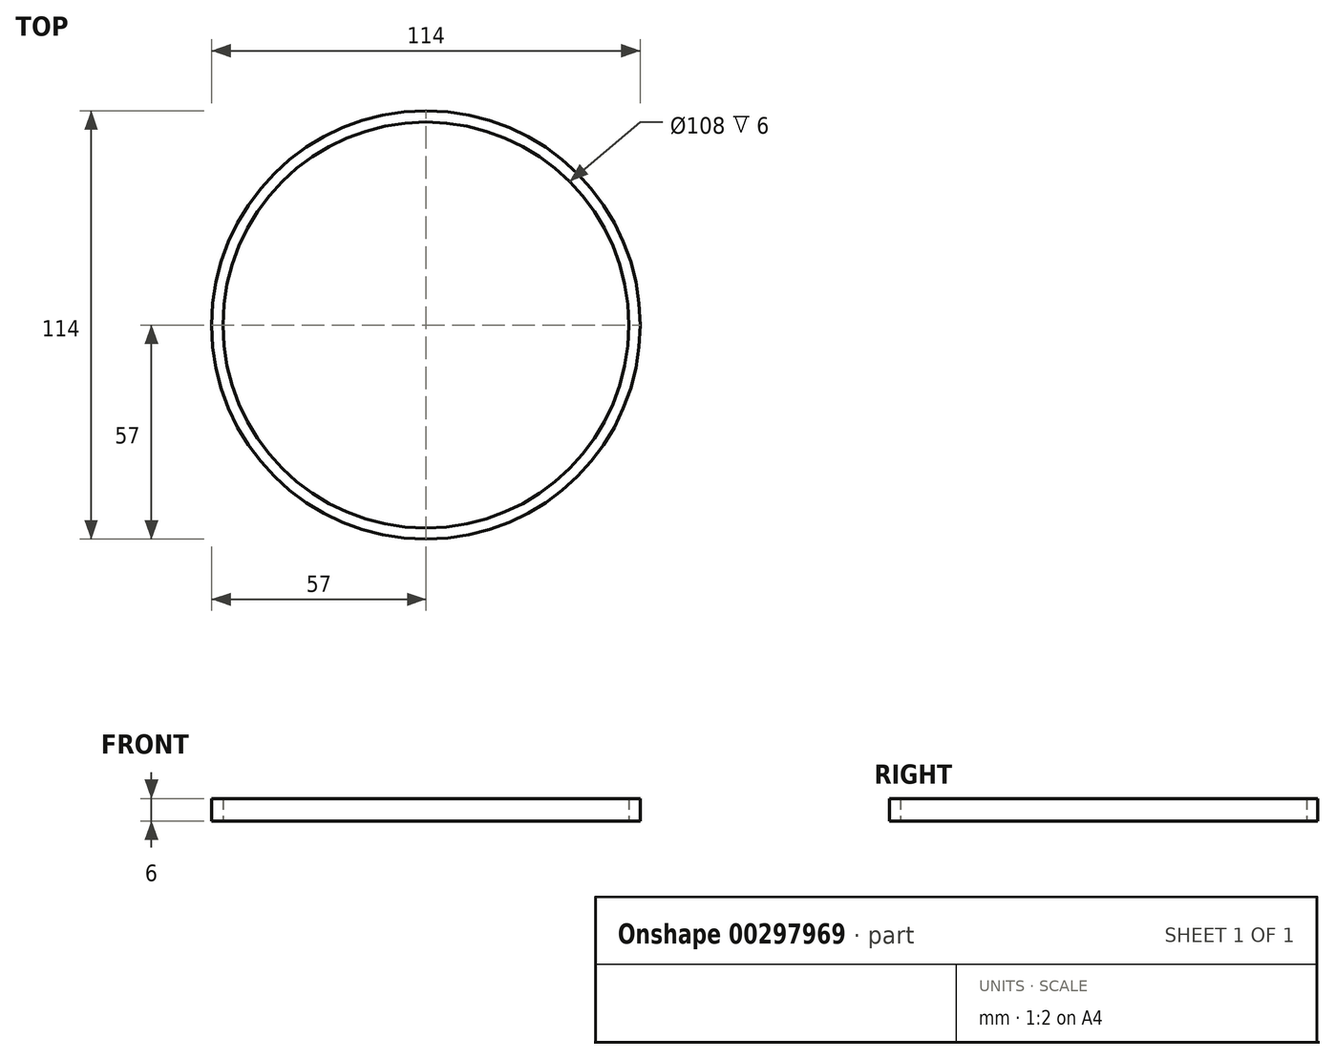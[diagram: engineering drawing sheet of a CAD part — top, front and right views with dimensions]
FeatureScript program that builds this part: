
annotation { "Feature Type Name" : "Feature", "Feature Type Description" : "" }
export const myFeature = defineFeature(function(context is Context, id is Id, definition is map)
    precondition{}
    {
        {
            var Q0;
            Q0=qCreatedBy(makeId("Front.planeOp"),FACE);
            var sketch = newSketch(context, id + "F0", { "sketchPlane" : qUnion([Q0])});
            skLineSegment(sketch, "E0.bottom", {"start": v(54, 0) * mm, "end": v(57, 0) * mm});
            skLineSegment(sketch, "E0.top", {"start": v(54, 6) * mm, "end": v(57, 6) * mm});
            skLineSegment(sketch, "E0.left", {"start": v(54, 0) * mm, "end": v(54, 6) * mm});
            skLineSegment(sketch, "E0.right", {"start": v(57, 0) * mm, "end": v(57, 6) * mm});
            skLineSegment(sketch, "E1", {"start": v(0, -8.33) * mm, "end": v(0, 13.44) * mm, "construction": true});
            skSolve(sketch);
        }
        {
            var Q0;
            Q0=makeQuery(id+"F0.imprint","IMPRINT",FACE,{"disambiguationData":[TD([[makeQuery(id+"F0.imprint","IMPRINT",EDGE,{"derivedFrom":sQuery(id+"F0.wireOp",EDGE,"E0.bottom")}),1.0]])]});
            var Q1;
            Q1=sQuery(id+"F0.wireOp",EDGE,"E1");
            revolve(context, id + "F1", {"entities" : qUnion([Q0]), "axis" : qUnion([Q1]), "revolveType" : RevolveType.FULL});
        }
    });
